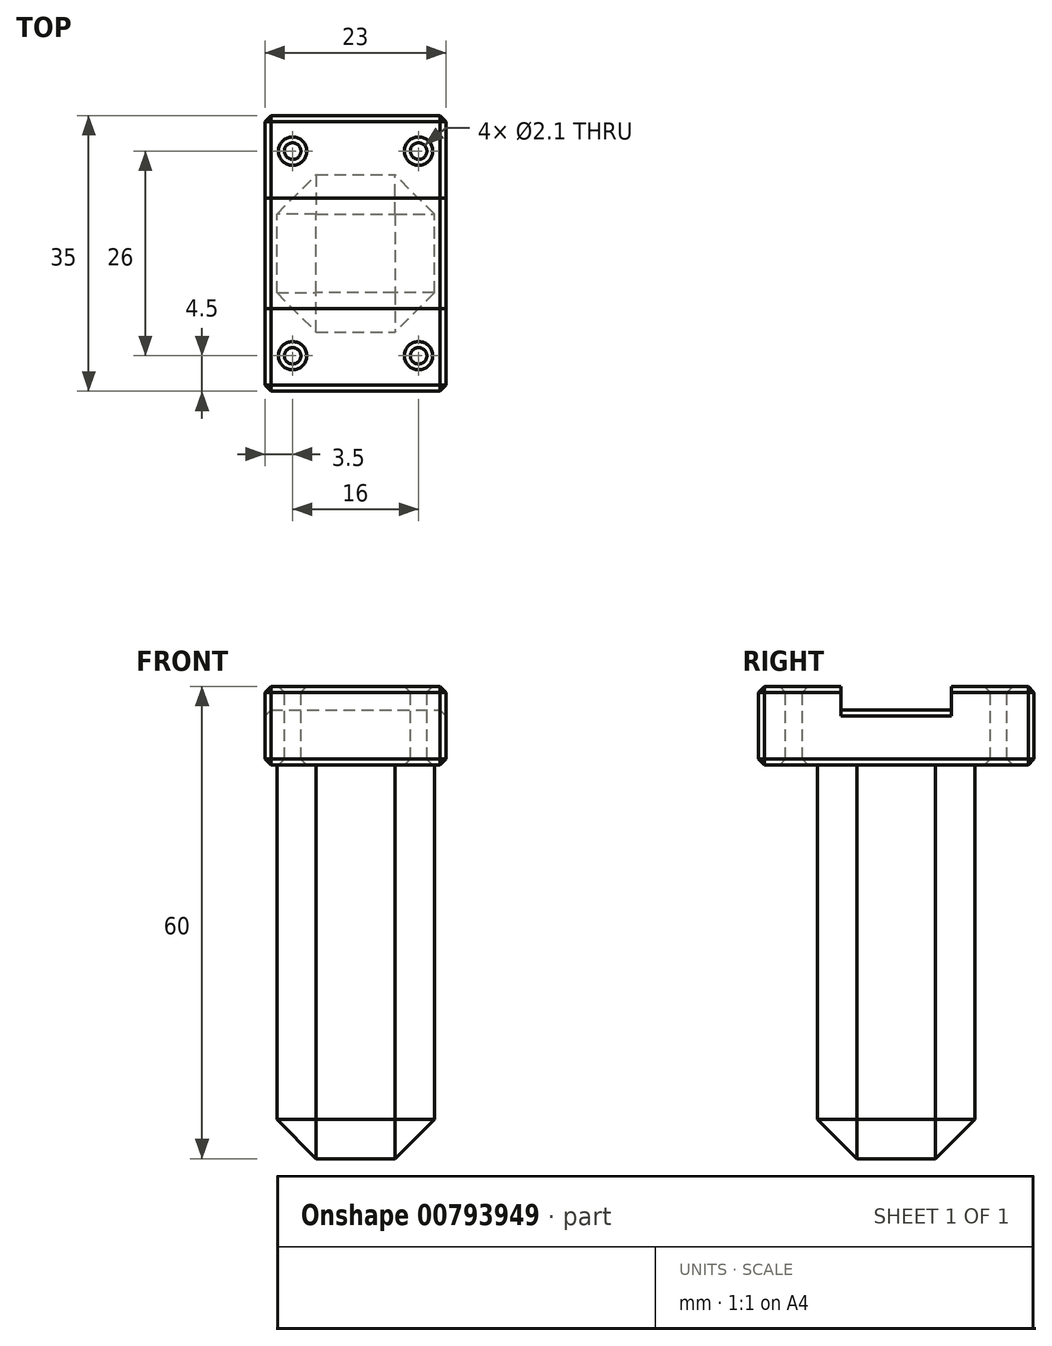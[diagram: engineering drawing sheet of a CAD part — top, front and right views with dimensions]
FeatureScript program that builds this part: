
annotation { "Feature Type Name" : "Feature", "Feature Type Description" : "" }
export const myFeature = defineFeature(function(context is Context, id is Id, definition is map)
    precondition{}
    {
        {
            var Q0;
            Q0=qCreatedBy(makeId("Top.planeOp"),FACE);
            var sketch = newSketch(context, id + "F0", { "sketchPlane" : qUnion([Q0])});
            skLineSegment(sketch, "E0.bottom", {"start": v(-11.5, 17.5) * mm, "end": v(11.5, 17.5) * mm});
            skLineSegment(sketch, "E0.top", {"start": v(-11.5, -17.5) * mm, "end": v(11.5, -17.5) * mm});
            skLineSegment(sketch, "E0.left", {"start": v(-11.5, 17.5) * mm, "end": v(-11.5, -17.5) * mm});
            skLineSegment(sketch, "E0.right", {"start": v(11.5, 17.5) * mm, "end": v(11.5, -17.5) * mm});
            skPoint(sketch, "E1", {"position": v(0, 17.5) * mm});
            skPoint(sketch, "E2", {"position": v(-11.5, 0) * mm});
            skCircle(sketch, "E3", {"center": v(-8, 13) * mm, "radius": 1.05 * mm});
            skCircle(sketch, "E4", {"center": v(8, 13) * mm, "radius": 1.05 * mm});
            skLineSegment(sketch, "E5", {"start": v(-8, 13) * mm, "end": v(8, 13) * mm});
            skPoint(sketch, "E6", {"position": v(0, 13) * mm});
            skLineSegment(sketch, "E7.MirrorCS", {"start": v(-8, -13) * mm, "end": v(8, -13) * mm});
            skPoint(sketch, "E8.MirrorP", {"position": v(0, -13) * mm});
            skCircle(sketch, "E9.MirrorC", {"center": v(8, -13) * mm, "radius": 1.05 * mm});
            skCircle(sketch, "E10.MirrorC", {"center": v(-8, -13) * mm, "radius": 1.05 * mm});
            skLineSegment(sketch, "E11", {"start": v(-11.5, 7) * mm, "end": v(11.5, 7) * mm});
            skLineSegment(sketch, "E12.MirrorCS", {"start": v(-11.5, -7) * mm, "end": v(11.5, -7) * mm});
            skSolve(sketch);
        }
        {
            var Q0;
            {var subQ1=sQuery(id+"F0.wireOp",EDGE,"E0.bottom");Q0=makeQuery(id+"F0.imprint","IMPRINT",FACE,{"disambiguationData":[TD([[makeQuery(id+"F0.imprint","IMPRINT",EDGE,{"derivedFrom":subQ1}),-1.0]])]});}
            var Q1;
            {var subQ1=sQuery(id+"F0.wireOp",EDGE,"E0.top");Q1=makeQuery(id+"F0.imprint","IMPRINT",FACE,{"disambiguationData":[TD([[makeQuery(id+"F0.imprint","IMPRINT",EDGE,{"derivedFrom":subQ1}),1.0]])]});}
            var Q2;
            {var subQ0=sQuery(id+"F0.wireOp",EDGE,"E11");Q2=makeQuery(id+"F0.imprint","IMPRINT",FACE,{"disambiguationData":[TD([[makeQuery(id+"F0.imprint","IMPRINT",EDGE,{"derivedFrom":subQ0}),-1.0]])]});}
            extrude(context, id + "F1", {"entities" : qUnion([Q0, Q1, Q2]), "oppositeDirection" : true, "depth" : 7 * mm, "offsetDistance" : 25 * mm});
        }
        {
            var Q0;
            {var subQ1=sQuery(id+"F0.wireOp",EDGE,"E0.bottom");Q0=makeQuery(id+"F0.imprint","IMPRINT",FACE,{"disambiguationData":[TD([[makeQuery(id+"F0.imprint","IMPRINT",EDGE,{"derivedFrom":subQ1}),-1.0]])]});}
            var Q1;
            {var subQ1=sQuery(id+"F0.wireOp",EDGE,"E0.top");Q1=makeQuery(id+"F0.imprint","IMPRINT",FACE,{"disambiguationData":[TD([[makeQuery(id+"F0.imprint","IMPRINT",EDGE,{"derivedFrom":subQ1}),1.0]])]});}
            extrude(context, id + "F2", {"entities" : qUnion([Q0, Q1]), "operationType" : NewBodyOperationType.ADD, "depth" : 3 * mm, "offsetDistance" : 25 * mm});
        }
        {
            var Q0;
            Q0=makeQuery(id+"F1.opExtrude","CAP_FACE",FACE,{"disambiguationData":[OSD([sQuery(id+"F0.wireOp",EDGE,"E0.bottom"),sQuery(id+"F0.wireOp",EDGE,"E0.top"),sQuery(id+"F0.wireOp",EDGE,"E0.left"),sQuery(id+"F0.wireOp",EDGE,"E0.right"),sQuery(id+"F0.wireOp",EDGE,"E3"),sQuery(id+"F0.wireOp",EDGE,"E4"),sQuery(id+"F0.wireOp",EDGE,"E9.MirrorC"),sQuery(id+"F0.wireOp",EDGE,"E10.MirrorC")])],"isStart":false});
            var sketch = newSketch(context, id + "F3", { "sketchPlane" : qUnion([Q0])});
            skLineSegment(sketch, "E13.bottom", {"start": v(-10, 10) * mm, "end": v(10, 10) * mm});
            skLineSegment(sketch, "E13.top", {"start": v(-10, -10) * mm, "end": v(10, -10) * mm});
            skLineSegment(sketch, "E13.left", {"start": v(-10, 10) * mm, "end": v(-10, -10) * mm});
            skLineSegment(sketch, "E13.right", {"start": v(10, 10) * mm, "end": v(10, -10) * mm});
            skPoint(sketch, "E14", {"position": v(0, 10) * mm});
            skPoint(sketch, "E15", {"position": v(-10, 0) * mm});
            skSolve(sketch);
        }
        {
            var Q0;
            Q0=makeQuery(id+"F3.imprint","IMPRINT",FACE,{"disambiguationData":[TD([[makeQuery(id+"F3.imprint","IMPRINT",EDGE,{"derivedFrom":sQuery(id+"F3.wireOp",EDGE,"E13.bottom")}),-1.0]])]});
            extrude(context, id + "F4", {"entities" : qUnion([Q0]), "operationType" : NewBodyOperationType.ADD, "depth" : 50 * mm, "offsetDistance" : 25 * mm});
        }
        {
            var Q0;
            Q0=makeQuery(id+"F4.opExtrude","CAP_EDGE",EDGE,{"disambiguationData":[OSD([sQuery(id+"F3.wireOp",EDGE,"E13.right")])],"isStart":true});
            var Q1;
            Q1=makeQuery(id+"F4.opExtrude","CAP_EDGE",EDGE,{"disambiguationData":[OSD([sQuery(id+"F3.wireOp",EDGE,"E13.bottom")])],"isStart":true});
            var Q2;
            Q2=makeQuery(id+"F4.opExtrude","CAP_EDGE",EDGE,{"disambiguationData":[OSD([sQuery(id+"F3.wireOp",EDGE,"E13.left")])],"isStart":true});
            var Q3;
            Q3=makeQuery(id+"F4.opExtrude","CAP_EDGE",EDGE,{"disambiguationData":[OSD([sQuery(id+"F3.wireOp",EDGE,"E13.top")])],"isStart":true});
            var Q4;
            Q4=makeQuery(id+"F2.opExtrude","CAP_EDGE",EDGE,{"disambiguationData":[OSD([sQuery(id+"F0.wireOp",EDGE,"E12.MirrorCS")])],"isStart":true});
            var Q5;
            Q5=makeQuery(id+"F2.opExtrude","CAP_EDGE",EDGE,{"disambiguationData":[OSD([sQuery(id+"F0.wireOp",EDGE,"E11")])],"isStart":true});
            var Q6;
            Q6=makeQuery(id+"F1.opExtrude","CAP_EDGE",EDGE,{"disambiguationData":[OSD([sQuery(id+"F0.wireOp",EDGE,"E0.left")])],"isStart":true});
            var Q7;
            Q7=makeQuery(id+"F1.opExtrude","CAP_EDGE",EDGE,{"disambiguationData":[OSD([sQuery(id+"F0.wireOp",EDGE,"E0.right")])],"isStart":true});
            var Q8;
            Q8=makeQuery(id+"F2.opExtrude","CAP_EDGE",EDGE,{"disambiguationData":[OSD([sQuery(id+"F0.wireOp",EDGE,"E0.bottom")])],"isStart":false});
            var Q9;
            {var subQ0=sQuery(id+"F0.wireOp",EDGE,"E0.left");Q9=makeQuery(id+"F2.opExtrude","CAP_EDGE",EDGE,{"disambiguationData":[OSD([subQ0]),TDD([makeQuery(id+"F0.imprint","IMPRINT",EDGE,{"disambiguationData":[TD([[makeQuery(id+"F0.imprint","INTERSECT",VERTEX,{"derivedFrom":[sQuery(id+"F0.wireOp",EDGE,"E0.bottom"),subQ0]}),-1.0]])],"derivedFrom":subQ0})])],"isStart":false});}
            var Q10;
            {var subQ0=sQuery(id+"F0.wireOp",EDGE,"E0.right");Q10=makeQuery(id+"F2.opExtrude","CAP_EDGE",EDGE,{"disambiguationData":[OSD([subQ0]),TDD([makeQuery(id+"F0.imprint","IMPRINT",EDGE,{"disambiguationData":[TD([[makeQuery(id+"F0.imprint","INTERSECT",VERTEX,{"derivedFrom":[sQuery(id+"F0.wireOp",EDGE,"E0.bottom"),subQ0]}),-1.0]])],"derivedFrom":subQ0})])],"isStart":false});}
            var Q11;
            {var subQ0=sQuery(id+"F0.wireOp",EDGE,"E0.right");Q11=makeQuery(id+"F2.opExtrude","CAP_EDGE",EDGE,{"disambiguationData":[OSD([subQ0]),TDD([makeQuery(id+"F0.imprint","IMPRINT",EDGE,{"disambiguationData":[TD([[makeQuery(id+"F0.imprint","INTERSECT",VERTEX,{"derivedFrom":[sQuery(id+"F0.wireOp",EDGE,"E0.top"),subQ0]}),1.0]])],"derivedFrom":subQ0})])],"isStart":false});}
            var Q12;
            Q12=makeQuery(id+"F2.opExtrude","CAP_EDGE",EDGE,{"disambiguationData":[OSD([sQuery(id+"F0.wireOp",EDGE,"E0.top")])],"isStart":false});
            var Q13;
            {var subQ0=sQuery(id+"F0.wireOp",EDGE,"E0.left");Q13=makeQuery(id+"F2.opExtrude","CAP_EDGE",EDGE,{"disambiguationData":[OSD([subQ0]),TDD([makeQuery(id+"F0.imprint","IMPRINT",EDGE,{"disambiguationData":[TD([[makeQuery(id+"F0.imprint","INTERSECT",VERTEX,{"derivedFrom":[sQuery(id+"F0.wireOp",EDGE,"E0.top"),subQ0]}),1.0]])],"derivedFrom":subQ0})])],"isStart":false});}
            var Q14;
            Q14=makeQuery(id+"F1.opExtrude","CAP_EDGE",EDGE,{"disambiguationData":[OSD([sQuery(id+"F0.wireOp",EDGE,"E0.bottom")])],"isStart":false});
            var Q15;
            Q15=makeQuery(id+"F1.opExtrude","CAP_EDGE",EDGE,{"disambiguationData":[OSD([sQuery(id+"F0.wireOp",EDGE,"E0.top")])],"isStart":false});
            var Q16;
            Q16=makeQuery(id+"F2.opExtrude","CAP_EDGE",EDGE,{"disambiguationData":[OSD([sQuery(id+"F0.wireOp",EDGE,"E3")])],"isStart":false});
            var Q17;
            Q17=makeQuery(id+"F2.opExtrude","CAP_EDGE",EDGE,{"disambiguationData":[OSD([sQuery(id+"F0.wireOp",EDGE,"E4")])],"isStart":false});
            var Q18;
            Q18=makeQuery(id+"F2.opExtrude","CAP_EDGE",EDGE,{"disambiguationData":[OSD([sQuery(id+"F0.wireOp",EDGE,"E10.MirrorC")])],"isStart":false});
            var Q19;
            Q19=makeQuery(id+"F2.opExtrude","CAP_EDGE",EDGE,{"disambiguationData":[OSD([sQuery(id+"F0.wireOp",EDGE,"E9.MirrorC")])],"isStart":false});
            var Q20;
            Q20=makeQuery(id+"F1.opExtrude","CAP_EDGE",EDGE,{"disambiguationData":[OSD([sQuery(id+"F0.wireOp",EDGE,"E10.MirrorC")])],"isStart":false});
            var Q21;
            Q21=makeQuery(id+"F1.opExtrude","CAP_EDGE",EDGE,{"disambiguationData":[OSD([sQuery(id+"F0.wireOp",EDGE,"E9.MirrorC")])],"isStart":false});
            var Q22;
            Q22=makeQuery(id+"F1.opExtrude","CAP_EDGE",EDGE,{"disambiguationData":[OSD([sQuery(id+"F0.wireOp",EDGE,"E3")])],"isStart":false});
            var Q23;
            Q23=makeQuery(id+"F1.opExtrude","CAP_EDGE",EDGE,{"disambiguationData":[OSD([sQuery(id+"F0.wireOp",EDGE,"E4")])],"isStart":false});
            var Q24;
            Q24=makeQuery(id+"F1.opExtrude","CAP_EDGE",EDGE,{"disambiguationData":[OSD([sQuery(id+"F0.wireOp",EDGE,"E0.left")])],"isStart":false});
            var Q25;
            Q25=makeQuery(id+"F1.opExtrude","CAP_EDGE",EDGE,{"disambiguationData":[OSD([sQuery(id+"F0.wireOp",EDGE,"E0.right")])],"isStart":false});
            var Q26;
            {var subQ0=sQuery(id+"F0.wireOp",EDGE,"E0.left");var subQ1=sQuery(id+"F0.wireOp",EDGE,"E0.bottom");Q26=makeQuery(id+"F2.boolean.opBoolean","MERGE",EDGE,{"derivedFrom":[makeQuery(id+"F1.opExtrude","SWEPT_EDGE",EDGE,{"disambiguationData":[OSD([subQ1,subQ0])]}),makeQuery(id+"F2.opExtrude","SWEPT_EDGE",EDGE,{"disambiguationData":[OSD([subQ1,subQ0])]})]});}
            var Q27;
            {var subQ0=sQuery(id+"F0.wireOp",EDGE,"E0.right");var subQ1=sQuery(id+"F0.wireOp",EDGE,"E0.bottom");Q27=makeQuery(id+"F2.boolean.opBoolean","MERGE",EDGE,{"derivedFrom":[makeQuery(id+"F1.opExtrude","SWEPT_EDGE",EDGE,{"disambiguationData":[OSD([subQ1,subQ0])]}),makeQuery(id+"F2.opExtrude","SWEPT_EDGE",EDGE,{"disambiguationData":[OSD([subQ1,subQ0])]})]});}
            var Q28;
            {var subQ0=sQuery(id+"F0.wireOp",EDGE,"E0.right");var subQ1=sQuery(id+"F0.wireOp",EDGE,"E0.top");Q28=makeQuery(id+"F2.boolean.opBoolean","MERGE",EDGE,{"derivedFrom":[makeQuery(id+"F1.opExtrude","SWEPT_EDGE",EDGE,{"disambiguationData":[OSD([subQ1,subQ0])]}),makeQuery(id+"F2.opExtrude","SWEPT_EDGE",EDGE,{"disambiguationData":[OSD([subQ1,subQ0])]})]});}
            var Q29;
            {var subQ0=sQuery(id+"F0.wireOp",EDGE,"E0.left");var subQ1=sQuery(id+"F0.wireOp",EDGE,"E0.top");Q29=makeQuery(id+"F2.boolean.opBoolean","MERGE",EDGE,{"derivedFrom":[makeQuery(id+"F1.opExtrude","SWEPT_EDGE",EDGE,{"disambiguationData":[OSD([subQ1,subQ0])]}),makeQuery(id+"F2.opExtrude","SWEPT_EDGE",EDGE,{"disambiguationData":[OSD([subQ1,subQ0])]})]});}
            chamfer(context, id + "F5", {"entities" : qUnion([Q0, Q1, Q2, Q3, Q4, Q5, Q6, Q7, Q8, Q9, Q10, Q11, Q12, Q13, Q14, Q15, Q16, Q17, Q18, Q19, Q20, Q21, Q22, Q23, Q24, Q25, Q26, Q27, Q28, Q29]), "width" : 0.75 * mm, "tangentPropagation" : true});
        }
        {
            var Q0;
            Q0=makeQuery(id+"F4.opExtrude","SWEPT_EDGE",EDGE,{"disambiguationData":[OSD([sQuery(id+"F3.wireOp",EDGE,"E13.top"),sQuery(id+"F3.wireOp",EDGE,"E13.left")])]});
            var Q1;
            Q1=makeQuery(id+"F4.opExtrude","SWEPT_EDGE",EDGE,{"disambiguationData":[OSD([sQuery(id+"F3.wireOp",EDGE,"E13.bottom"),sQuery(id+"F3.wireOp",EDGE,"E13.left")])]});
            var Q2;
            Q2=makeQuery(id+"F4.opExtrude","SWEPT_EDGE",EDGE,{"disambiguationData":[OSD([sQuery(id+"F3.wireOp",EDGE,"E13.bottom"),sQuery(id+"F3.wireOp",EDGE,"E13.right")])]});
            var Q3;
            Q3=makeQuery(id+"F4.opExtrude","SWEPT_EDGE",EDGE,{"disambiguationData":[OSD([sQuery(id+"F3.wireOp",EDGE,"E13.top"),sQuery(id+"F3.wireOp",EDGE,"E13.right")])]});
            var Q4;
            Q4=makeQuery(id+"F4.opExtrude","CAP_EDGE",EDGE,{"disambiguationData":[OSD([sQuery(id+"F3.wireOp",EDGE,"E13.bottom")])],"isStart":false});
            var Q5;
            Q5=makeQuery(id+"F4.opExtrude","CAP_EDGE",EDGE,{"disambiguationData":[OSD([sQuery(id+"F3.wireOp",EDGE,"E13.right")])],"isStart":false});
            var Q6;
            Q6=makeQuery(id+"F4.opExtrude","CAP_EDGE",EDGE,{"disambiguationData":[OSD([sQuery(id+"F3.wireOp",EDGE,"E13.top")])],"isStart":false});
            var Q7;
            Q7=makeQuery(id+"F4.opExtrude","CAP_EDGE",EDGE,{"disambiguationData":[OSD([sQuery(id+"F3.wireOp",EDGE,"E13.left")])],"isStart":false});
            chamfer(context, id + "F6", {"entities" : qUnion([Q0, Q1, Q2, Q3, Q4, Q5, Q6, Q7]), "width" : 5 * mm, "tangentPropagation" : true});
        }
    });
